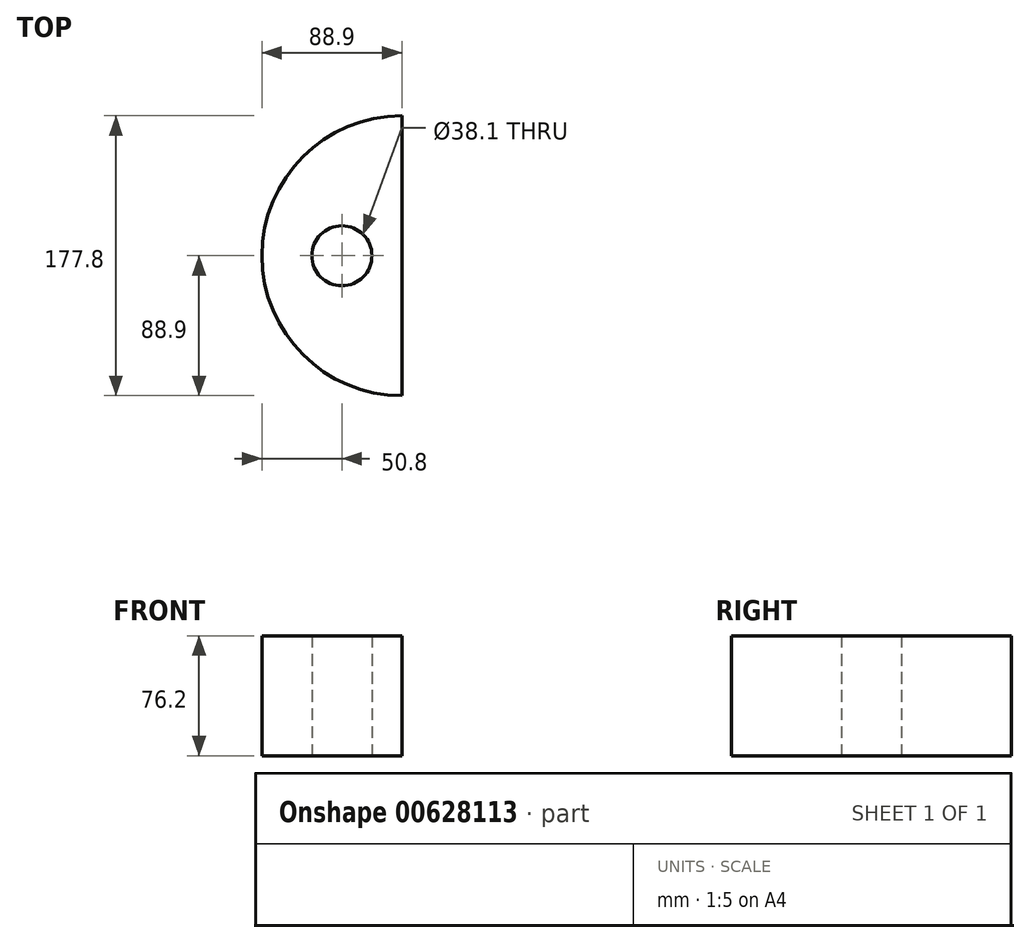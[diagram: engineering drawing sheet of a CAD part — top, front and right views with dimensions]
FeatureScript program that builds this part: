
annotation { "Feature Type Name" : "Feature", "Feature Type Description" : "" }
export const myFeature = defineFeature(function(context is Context, id is Id, definition is map)
    precondition{}
    {
        {
            var Q0;
            Q0=qCreatedBy(makeId("Top.planeOp"),FACE);
            var sketch = newSketch(context, id + "F0", { "sketchPlane" : qUnion([Q0])});
            skArc(sketch, "E0", {"start": v(0, 88.9) * mm, "mid": v(-88.9, 0) * mm, "end": v(0, -88.9) * mm});
            skLineSegment(sketch, "E1", {"start": v(0, 88.9) * mm, "end": v(0, -88.9) * mm});
            skCircle(sketch, "E2", {"center": v(-38.1, 0) * mm, "radius": 19.05 * mm});
            skSolve(sketch);
        }
        {
            var Q0;
            Q0=makeQuery(id+"F0.imprint","IMPRINT",FACE,{"disambiguationData":[TD([[makeQuery(id+"F0.imprint","IMPRINT",EDGE,{"derivedFrom":sQuery(id+"F0.wireOp",EDGE,"E0")}),1.0]])]});
            extrude(context, id + "F1", {"entities" : qUnion([Q0]), "depth" : 76.2 * mm, "offsetDistance" : 25.4 * mm});
        }
    });
